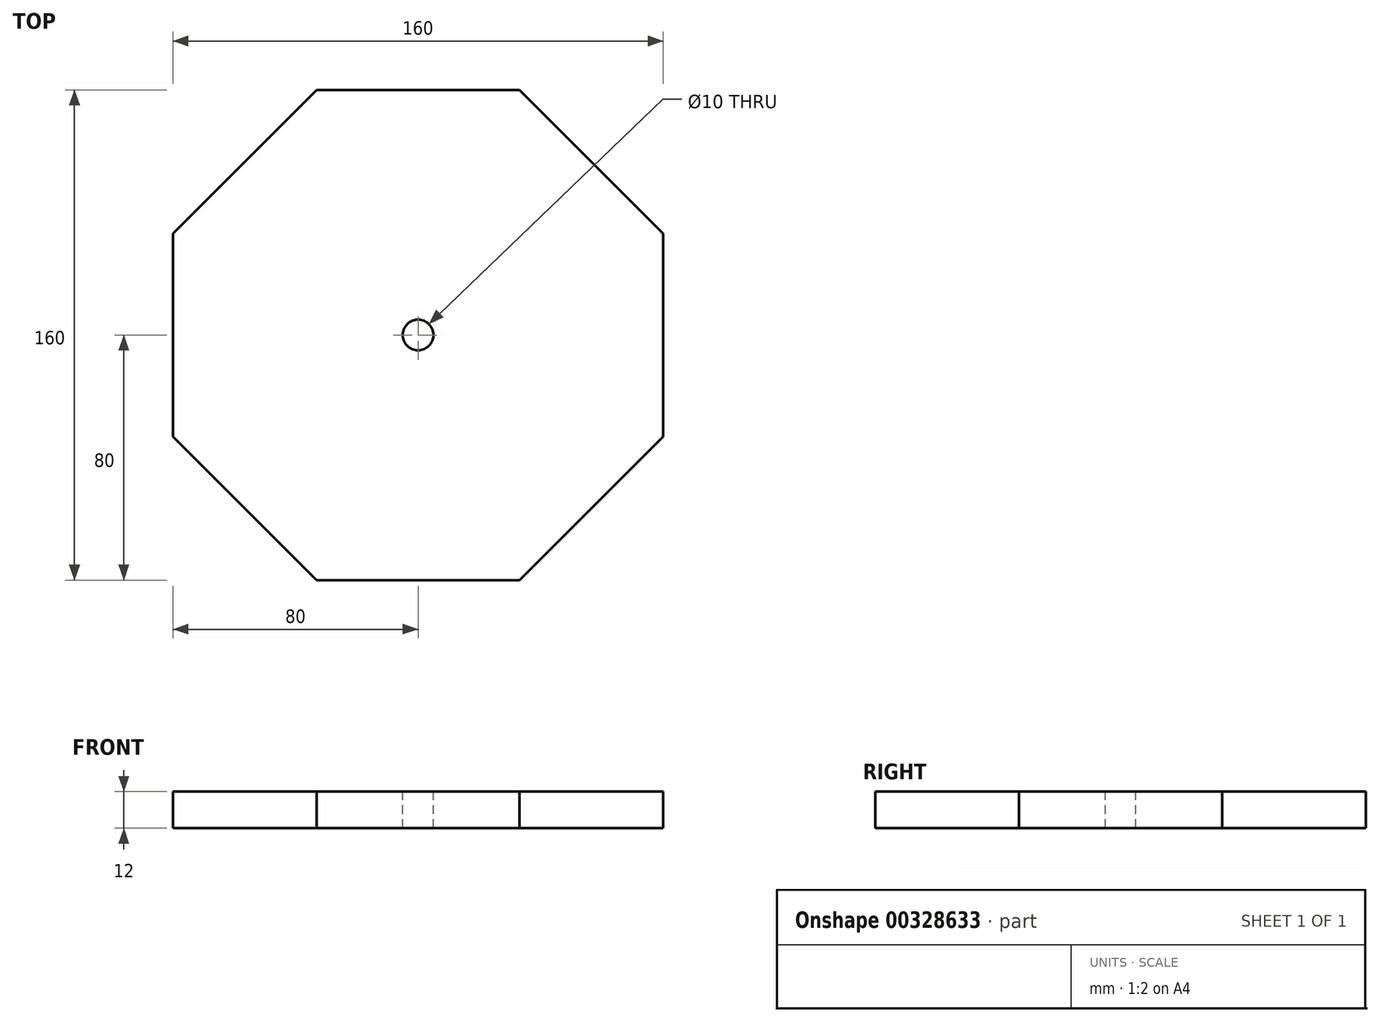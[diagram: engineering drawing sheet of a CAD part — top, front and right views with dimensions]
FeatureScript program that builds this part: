
annotation { "Feature Type Name" : "Feature", "Feature Type Description" : "" }
export const myFeature = defineFeature(function(context is Context, id is Id, definition is map)
    precondition{}
    {
        {
            var Q0;
            Q0=qCreatedBy(makeId("Top.planeOp"),FACE);
            var sketch = newSketch(context, id + "F0", { "sketchPlane" : qUnion([Q0])});
            skCircle(sketch, "E0.cCircle", {"center": v(0, 0) * mm, "radius": 80 * mm, "construction": true});
            skLineSegment(sketch, "E0.0", {"start": v(-33.14, 80) * mm, "end": v(33.14, 80) * mm});
            skLineSegment(sketch, "E0.1", {"start": v(33.14, 80) * mm, "end": v(80, 33.14) * mm});
            skLineSegment(sketch, "E0.2", {"start": v(80, 33.14) * mm, "end": v(80, -33.14) * mm});
            skLineSegment(sketch, "E0.3", {"start": v(80, -33.14) * mm, "end": v(33.14, -80) * mm});
            skLineSegment(sketch, "E0.4", {"start": v(33.14, -80) * mm, "end": v(-33.14, -80) * mm});
            skLineSegment(sketch, "E0.5", {"start": v(-33.14, -80) * mm, "end": v(-80, -33.14) * mm});
            skLineSegment(sketch, "E0.6", {"start": v(-80, -33.14) * mm, "end": v(-80, 33.14) * mm});
            skLineSegment(sketch, "E0.7", {"start": v(-80, 33.14) * mm, "end": v(-33.14, 80) * mm});
            skPoint(sketch, "E0.0.midPoint", {"position": v(0, 80) * mm});
            skSolve(sketch);
        }
        {
            var Q0;
            Q0=qSketchRegion(id+"F0",true);
            extrude(context, id + "F1", {"entities" : qUnion([Q0]), "oppositeDirection" : true, "depth" : 12 * mm});
        }
        {
            var Q0;
            Q0=makeQuery(id+"F1.opExtrude","CAP_FACE",FACE,{"disambiguationData":[OSD([sQuery(id+"F0.wireOp",EDGE,"E0.0"),sQuery(id+"F0.wireOp",EDGE,"E0.1"),sQuery(id+"F0.wireOp",EDGE,"E0.2"),sQuery(id+"F0.wireOp",EDGE,"E0.3"),sQuery(id+"F0.wireOp",EDGE,"E0.4"),sQuery(id+"F0.wireOp",EDGE,"E0.5"),sQuery(id+"F0.wireOp",EDGE,"E0.6"),sQuery(id+"F0.wireOp",EDGE,"E0.7")])],"isStart":true});
            var sketch = newSketch(context, id + "F2", { "sketchPlane" : qUnion([Q0])});
            skLineSegment(sketch, "E1", {"start": v(-80, 0) * mm, "end": v(80, 0) * mm, "construction": true});
            skPoint(sketch, "E2", {"position": v(0, 0) * mm});
            skSolve(sketch);
        }
        {
            var Q0;
            Q0=sQuery(id+"F2.wireOp",VERTEX,"E2");
            var Q1;
            Q1=makeQuery(id+"F1.opExtrude","SWEPT_BODY",BODY,{"disambiguationData":[OSD([sQuery(id+"F0.wireOp",EDGE,"E0.0"),sQuery(id+"F0.wireOp",EDGE,"E0.1"),sQuery(id+"F0.wireOp",EDGE,"E0.2"),sQuery(id+"F0.wireOp",EDGE,"E0.3"),sQuery(id+"F0.wireOp",EDGE,"E0.4"),sQuery(id+"F0.wireOp",EDGE,"E0.5"),sQuery(id+"F0.wireOp",EDGE,"E0.6"),sQuery(id+"F0.wireOp",EDGE,"E0.7")])]});
            hole(context, id + "F3", {"style" : HoleStyle.SIMPLE, "endStyle" : HoleEndStyle.THROUGH, "holeDiameter" : 10 * mm, "tappedDepth" : 12 * mm, "tapClearance" : 3, "locations" : qUnion([Q0]), "scope" : qUnion([Q1])});
        }
    });
